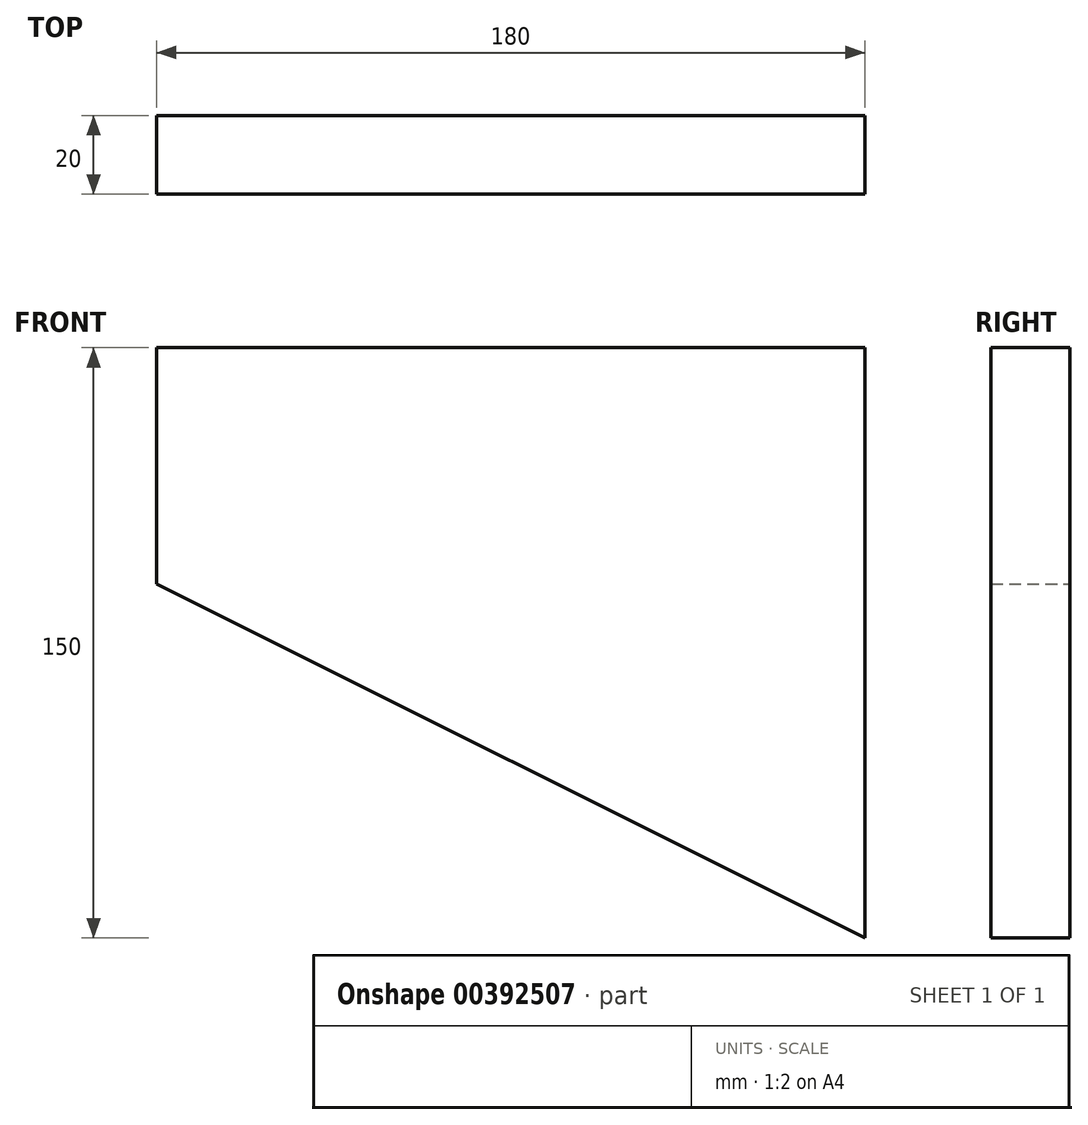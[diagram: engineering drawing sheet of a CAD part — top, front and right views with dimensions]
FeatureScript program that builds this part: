
annotation { "Feature Type Name" : "Feature", "Feature Type Description" : "" }
export const myFeature = defineFeature(function(context is Context, id is Id, definition is map)
    precondition{}
    {
        {
            var Q0;
            Q0=qCreatedBy(makeId("Front.planeOp"),FACE);
            var sketch = newSketch(context, id + "F0", { "sketchPlane" : qUnion([Q0])});
            skLineSegment(sketch, "E0", {"start": v(0, 0) * mm, "end": v(0, 150) * mm});
            skLineSegment(sketch, "E1", {"start": v(0, 150) * mm, "end": v(-180, 150) * mm});
            skLineSegment(sketch, "E2", {"start": v(-180, 150) * mm, "end": v(-180, 90) * mm});
            skLineSegment(sketch, "E3", {"start": v(-180, 90) * mm, "end": v(0, 0) * mm});
            skSolve(sketch);
        }
        {
            var Q0;
            Q0 = qSketchRegion(id + "F0", true);
            extrude(context, id + "F1", {"entities" : qUnion([Q0]), "depth" : 20 * mm});
        }
    });
